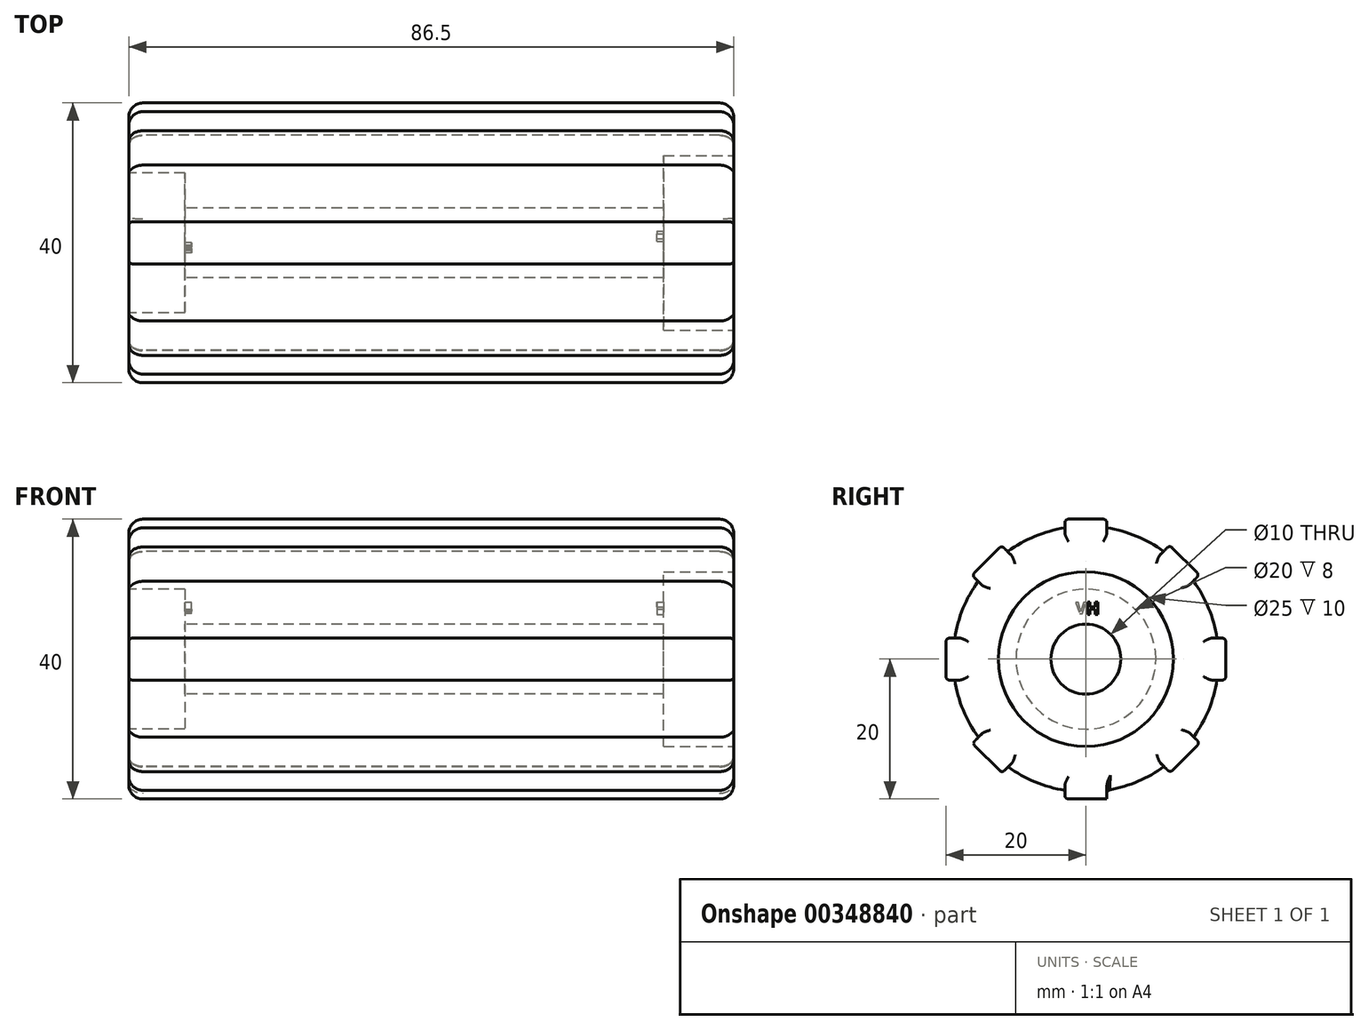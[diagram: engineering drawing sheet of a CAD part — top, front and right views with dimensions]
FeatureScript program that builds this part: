
annotation { "Feature Type Name" : "Feature", "Feature Type Description" : "" }
export const myFeature = defineFeature(function(context is Context, id is Id, definition is map)
    precondition{}
    {
        {
            var Q0;
            Q0=qCreatedBy(makeId("Right.planeOp"),FACE);
            var sketch = newSketch(context, id + "F0", { "sketchPlane" : qUnion([Q0])});
            skCircle(sketch, "E0", {"center": v(0, 0) * mm, "radius": 19 * mm});
            skCircle(sketch, "E1", {"center": v(0, 0) * mm, "radius": 5 * mm});
            skSolve(sketch);
        }
        {
            var Q0;
            Q0=makeQuery(id+"F0.imprint","IMPRINT",FACE,{"disambiguationData":[TD([[makeQuery(id+"F0.imprint","IMPRINT",EDGE,{"derivedFrom":sQuery(id+"F0.wireOp",EDGE,"E0")}),1.0]])]});
            extrude(context, id + "F1", {"entities" : qUnion([Q0]), "depth" : 86.5 * mm});
        }
        {
            var Q0;
            Q0=makeQuery(id+"F1.opExtrude","CAP_FACE",FACE,{"disambiguationData":[OSD([sQuery(id+"F0.wireOp",EDGE,"E0"),sQuery(id+"F0.wireOp",EDGE,"E1")])],"isStart":true});
            var sketch = newSketch(context, id + "F2", { "sketchPlane" : qUnion([Q0])});
            skCircle(sketch, "E2", {"center": v(0, 0) * mm, "radius": 10 * mm});
            skSolve(sketch);
        }
        {
            var Q0;
            Q0=makeQuery(id+"F2.imprint","IMPRINT",FACE,{"disambiguationData":[TD([[makeQuery(id+"F2.imprint","IMPRINT",EDGE,{"derivedFrom":sQuery(id+"F2.wireOp",EDGE,"E2")}),1.0]])]});
            extrude(context, id + "F3", {"entities" : qUnion([Q0]), "operationType" : NewBodyOperationType.REMOVE, "oppositeDirection" : true, "depth" : 8 * mm});
        }
        {
            var Q0;
            Q0=makeQuery(id+"F1.opExtrude","CAP_FACE",FACE,{"disambiguationData":[OSD([sQuery(id+"F0.wireOp",EDGE,"E0"),sQuery(id+"F0.wireOp",EDGE,"E1")])],"isStart":false});
            var sketch = newSketch(context, id + "F4", { "sketchPlane" : qUnion([Q0])});
            skCircle(sketch, "E3", {"center": v(0, 0) * mm, "radius": 10 * mm});
            skSolve(sketch);
        }
        {
            var Q0;
            Q0=makeQuery(id+"F4.imprint","IMPRINT",FACE,{"disambiguationData":[TD([[makeQuery(id+"F4.imprint","IMPRINT",EDGE,{"derivedFrom":sQuery(id+"F4.wireOp",EDGE,"E3")}),1.0]])]});
            extrude(context, id + "F5", {"entities" : qUnion([Q0]), "operationType" : NewBodyOperationType.REMOVE, "oppositeDirection" : true, "depth" : 10 * mm});
        }
        {
            var Q0;
            Q0=makeQuery(id+"F5.boolean.opBoolean","COPY",FACE,{"derivedFrom":makeQuery(id+"F5.opExtrude","CAP_FACE",FACE,{"disambiguationData":[OSD([sQuery(id+"F0.wireOp",EDGE,"E1"),sQuery(id+"F4.wireOp",EDGE,"E3")])],"isStart":false})});
            var sketch = newSketch(context, id + "F6", { "sketchPlane" : qUnion([Q0])});
            skText(sketch, "E4", { "text": "H", "fontName": "OpenSans-Bold.ttf"});
            const initialGuessF6  = {"E4": [0, 0.0064, 1, 0, 0.0018]};
            skSetInitialGuess(sketch, initialGuessF6);
            skSolve(sketch);
        }
        {
            var Q0;
            Q0=makeQuery(id+"F6.imprint","IMPRINT",FACE,{"disambiguationData":[TD([[makeQuery(id+"F6.imprint","IMPRINT",EDGE,{"derivedFrom":sQuery(id+"F6.wireOp",EDGE,"E4.sketch_text.stroke-0")}),-1.0]])]});
            extrude(context, id + "F7", {"entities" : qUnion([Q0]), "operationType" : NewBodyOperationType.REMOVE, "oppositeDirection" : true, "depth" : 1 * mm});
        }
        {
            var Q0;
            Q0=makeQuery(id+"F3.boolean.opBoolean","COPY",FACE,{"derivedFrom":makeQuery(id+"F3.opExtrude","CAP_FACE",FACE,{"disambiguationData":[OSD([sQuery(id+"F0.wireOp",EDGE,"E1"),sQuery(id+"F2.wireOp",EDGE,"E2")])],"isStart":false})});
            var sketch = newSketch(context, id + "F8", { "sketchPlane" : qUnion([Q0])});
            skText(sketch, "E5", { "text": "V", "fontName": "OpenSans-Bold.ttf"});
            const initialGuessF8  = {"E5": [0, 0.0065, 1, 0, 0.0016]};
            skSetInitialGuess(sketch, initialGuessF8);
            skSolve(sketch);
        }
        {
            var Q0;
            Q0 = qSketchRegion(id + "F8", true);
            extrude(context, id + "F9", {"entities" : qUnion([Q0]), "operationType" : NewBodyOperationType.REMOVE, "oppositeDirection" : true, "depth" : 1 * mm});
        }
        {
            var Q0;
            Q0=makeQuery(id+"F1.opExtrude","CAP_FACE",FACE,{"disambiguationData":[OSD([sQuery(id+"F0.wireOp",EDGE,"E0"),sQuery(id+"F0.wireOp",EDGE,"E1")])],"isStart":false});
            var sketch = newSketch(context, id + "F10", { "sketchPlane" : qUnion([Q0])});
            skCircle(sketch, "E6", {"center": v(0, 0) * mm, "radius": 12.5 * mm});
            skSolve(sketch);
        }
        {
            var Q0;
            Q0=makeQuery(id+"F10.imprint","IMPRINT",FACE,{"disambiguationData":[TD([[makeQuery(id+"F10.imprint","IMPRINT",EDGE,{"derivedFrom":sQuery(id+"F10.wireOp",EDGE,"E6")}),1.0]])]});
            extrude(context, id + "F11", {"entities" : qUnion([Q0]), "operationType" : NewBodyOperationType.REMOVE, "oppositeDirection" : true, "depth" : 10 * mm});
        }
        {
            var Q0;
            Q0=makeQuery(id+"F1.opExtrude","CAP_EDGE",EDGE,{"disambiguationData":[OSD([sQuery(id+"F0.wireOp",EDGE,"E0")])],"isStart":true});
            var Q1;
            Q1=makeQuery(id+"F1.opExtrude","CAP_EDGE",EDGE,{"disambiguationData":[OSD([sQuery(id+"F0.wireOp",EDGE,"E0")])],"isStart":false});
            fillet(context, id + "F12", {"entities" : qUnion([Q0, Q1]), "radius" : 2 * mm, "tangentPropagation" : true, "allowEdgeOverflow" : false});
        }
        {
            var Q0;
            Q0=makeQuery(id+"F1.opExtrude","CAP_FACE",FACE,{"disambiguationData":[OSD([sQuery(id+"F0.wireOp",EDGE,"E0"),sQuery(id+"F0.wireOp",EDGE,"E1")])],"isStart":false});
            var sketch = newSketch(context, id + "F13", { "sketchPlane" : qUnion([Q0])});
            skPoint(sketch, "E7.middle", {"position": v(0, 0) * mm});
            skLineSegment(sketch, "E8.top", {"start": v(-3, 14) * mm, "end": v(3, 14) * mm});
            skLineSegment(sketch, "E9.right", {"start": v(-14, 3) * mm, "end": v(-14, -3) * mm});
            skLineSegment(sketch, "E10.top", {"start": v(-3, -14) * mm, "end": v(3, -14) * mm});
            skPoint(sketch, "E11.endSnap0", {"position": v(-12, -12) * mm});
            skLineSegment(sketch, "E12", {"start": v(-7.8, 12) * mm, "end": v(-12.04, 7.75) * mm});
            skLineSegment(sketch, "E13", {"start": v(12, 7.8) * mm, "end": v(7.75, 12.04) * mm});
            skLineSegment(sketch, "E14", {"start": v(12.03, -7.76) * mm, "end": v(7.8, -12) * mm});
            skLineSegment(sketch, "E15", {"start": v(-7.76, -12.03) * mm, "end": v(-12, -7.8) * mm});
            skLineSegment(sketch, "E16", {"start": v(-20, 3) * mm, "end": v(-20, -3) * mm});
            skLineSegment(sketch, "E17", {"start": v(-20, 3) * mm, "end": v(-14, 3) * mm});
            skLineSegment(sketch, "E18", {"start": v(-20, -3) * mm, "end": v(-14, -3) * mm});
            skLineSegment(sketch, "E19", {"start": v(-12.04, 16.23) * mm, "end": v(-16.29, 12) * mm});
            skLineSegment(sketch, "E20", {"start": v(-12.04, 16.23) * mm, "end": v(-7.8, 12) * mm});
            skLineSegment(sketch, "E21", {"start": v(-16.29, 12) * mm, "end": v(-12.04, 7.75) * mm});
            skLineSegment(sketch, "E22.bottom", {"start": v(3, 20) * mm, "end": v(-3, 20) * mm});
            skLineSegment(sketch, "E22.top", {"start": v(3, 14) * mm, "end": v(-3, 14) * mm});
            skLineSegment(sketch, "E22.left", {"start": v(3, 20) * mm, "end": v(3, 14) * mm});
            skLineSegment(sketch, "E23", {"start": v(-3, 20) * mm, "end": v(-3, 14) * mm});
            skLineSegment(sketch, "E24", {"start": v(12, 16.29) * mm, "end": v(7.75, 12.04) * mm});
            skLineSegment(sketch, "E25", {"start": v(12, 16.29) * mm, "end": v(16.23, 12.04) * mm});
            skLineSegment(sketch, "E26", {"start": v(16.23, 12.04) * mm, "end": v(12, 7.8) * mm});
            skLineSegment(sketch, "E27", {"start": v(20, 3) * mm, "end": v(20, -3) * mm});
            skLineSegment(sketch, "E28.bottom", {"start": v(20, 3) * mm, "end": v(14, 3) * mm});
            skLineSegment(sketch, "E28.top", {"start": v(20, -3) * mm, "end": v(14, -3) * mm});
            skLineSegment(sketch, "E28.right", {"start": v(14, 3) * mm, "end": v(14, -3) * mm});
            skLineSegment(sketch, "E29", {"start": v(16.28, -12) * mm, "end": v(12.05, -16.24) * mm});
            skLineSegment(sketch, "E30", {"start": v(7.8, -12) * mm, "end": v(12.05, -16.24) * mm});
            skLineSegment(sketch, "E31", {"start": v(16.28, -12) * mm, "end": v(12.03, -7.76) * mm});
            skLineSegment(sketch, "E32", {"start": v(-16.24, -12.05) * mm, "end": v(-12, -16.28) * mm});
            skLineSegment(sketch, "E33", {"start": v(-12, -16.28) * mm, "end": v(-7.76, -12.03) * mm});
            skLineSegment(sketch, "E34", {"start": v(-12, -7.8) * mm, "end": v(-16.24, -12.05) * mm});
            skLineSegment(sketch, "E35", {"start": v(3, -20) * mm, "end": v(-3, -20) * mm});
            skLineSegment(sketch, "E36", {"start": v(-3, -20) * mm, "end": v(-3, -14) * mm});
            skLineSegment(sketch, "E37", {"start": v(3, -14) * mm, "end": v(3, -20) * mm});
            skSolve(sketch);
        }
        {
            var Q0;
            {var subQ0=sQuery(id+"F13.wireOp",EDGE,"E19");Q0=makeQuery(id+"F13.imprint","IMPRINT",FACE,{"disambiguationData":[TD([[makeQuery(id+"F13.imprint","IMPRINT",EDGE,{"derivedFrom":subQ0}),1.0]])]});}
            var Q1;
            {var subQ0=sQuery(id+"F13.wireOp",EDGE,"E22.bottom");Q1=makeQuery(id+"F13.imprint","IMPRINT",FACE,{"disambiguationData":[TD([[makeQuery(id+"F13.imprint","IMPRINT",EDGE,{"derivedFrom":subQ0}),1.0]])]});}
            var Q2;
            {var subQ0=sQuery(id+"F13.wireOp",EDGE,"E25");Q2=makeQuery(id+"F13.imprint","IMPRINT",FACE,{"disambiguationData":[TD([[makeQuery(id+"F13.imprint","IMPRINT",EDGE,{"derivedFrom":subQ0}),-1.0]])]});}
            var Q3;
            {var subQ0=sQuery(id+"F13.wireOp",EDGE,"E27");Q3=makeQuery(id+"F13.imprint","IMPRINT",FACE,{"disambiguationData":[TD([[makeQuery(id+"F13.imprint","IMPRINT",EDGE,{"derivedFrom":subQ0}),-1.0]])]});}
            var Q4;
            {var subQ0=sQuery(id+"F13.wireOp",EDGE,"E29");Q4=makeQuery(id+"F13.imprint","IMPRINT",FACE,{"disambiguationData":[TD([[makeQuery(id+"F13.imprint","IMPRINT",EDGE,{"derivedFrom":subQ0}),-1.0]])]});}
            var Q5;
            {var subQ0=sQuery(id+"F13.wireOp",EDGE,"E16");Q5=makeQuery(id+"F13.imprint","IMPRINT",FACE,{"disambiguationData":[TD([[makeQuery(id+"F13.imprint","IMPRINT",EDGE,{"derivedFrom":subQ0}),1.0]])]});}
            var Q6;
            {var subQ0=sQuery(id+"F13.wireOp",EDGE,"E35");Q6=makeQuery(id+"F13.imprint","IMPRINT",FACE,{"disambiguationData":[TD([[makeQuery(id+"F13.imprint","IMPRINT",EDGE,{"derivedFrom":subQ0}),-1.0]])]});}
            var Q7;
            {var subQ0=sQuery(id+"F13.wireOp",EDGE,"E32");Q7=makeQuery(id+"F13.imprint","IMPRINT",FACE,{"disambiguationData":[TD([[makeQuery(id+"F13.imprint","IMPRINT",EDGE,{"derivedFrom":subQ0}),1.0]])]});}
            extrude(context, id + "F14", {"entities" : qUnion([Q0, Q1, Q2, Q3, Q4, Q5, Q6, Q7]), "operationType" : NewBodyOperationType.ADD, "oppositeDirection" : true, "depth" : 86.5 * mm});
        }
        {
            var Q0;
            Q0=makeQuery(id+"F14.opExtrude","CAP_EDGE",EDGE,{"disambiguationData":[OSD([sQuery(id+"F13.wireOp",EDGE,"E19")])],"isStart":true});
            var Q1;
            Q1=makeQuery(id+"F14.opExtrude","CAP_EDGE",EDGE,{"disambiguationData":[OSD([sQuery(id+"F13.wireOp",EDGE,"E22.bottom")])],"isStart":true});
            var Q2;
            Q2=makeQuery(id+"F14.opExtrude","CAP_EDGE",EDGE,{"disambiguationData":[OSD([sQuery(id+"F13.wireOp",EDGE,"E25")])],"isStart":true});
            var Q3;
            Q3=makeQuery(id+"F14.opExtrude","CAP_EDGE",EDGE,{"disambiguationData":[OSD([sQuery(id+"F13.wireOp",EDGE,"E27")])],"isStart":true});
            var Q4;
            Q4=makeQuery(id+"F14.opExtrude","CAP_EDGE",EDGE,{"disambiguationData":[OSD([sQuery(id+"F13.wireOp",EDGE,"E29")])],"isStart":true});
            var Q5;
            Q5=makeQuery(id+"F14.opExtrude","CAP_EDGE",EDGE,{"disambiguationData":[OSD([sQuery(id+"F13.wireOp",EDGE,"E35")])],"isStart":true});
            var Q6;
            Q6=makeQuery(id+"F14.opExtrude","CAP_EDGE",EDGE,{"disambiguationData":[OSD([sQuery(id+"F13.wireOp",EDGE,"E32")])],"isStart":true});
            var Q7;
            Q7=makeQuery(id+"F14.opExtrude","CAP_EDGE",EDGE,{"disambiguationData":[OSD([sQuery(id+"F13.wireOp",EDGE,"E16")])],"isStart":true});
            var Q8;
            Q8=makeQuery(id+"F14.opExtrude","CAP_EDGE",EDGE,{"disambiguationData":[OSD([sQuery(id+"F13.wireOp",EDGE,"E25")])],"isStart":false});
            var Q9;
            Q9=makeQuery(id+"F14.opExtrude","CAP_EDGE",EDGE,{"disambiguationData":[OSD([sQuery(id+"F13.wireOp",EDGE,"E22.bottom")])],"isStart":false});
            var Q10;
            Q10=makeQuery(id+"F14.opExtrude","CAP_EDGE",EDGE,{"disambiguationData":[OSD([sQuery(id+"F13.wireOp",EDGE,"E19")])],"isStart":false});
            var Q11;
            Q11=makeQuery(id+"F14.opExtrude","CAP_EDGE",EDGE,{"disambiguationData":[OSD([sQuery(id+"F13.wireOp",EDGE,"E16")])],"isStart":false});
            var Q12;
            Q12=makeQuery(id+"F14.opExtrude","CAP_EDGE",EDGE,{"disambiguationData":[OSD([sQuery(id+"F13.wireOp",EDGE,"E32")])],"isStart":false});
            var Q13;
            Q13=makeQuery(id+"F14.opExtrude","CAP_EDGE",EDGE,{"disambiguationData":[OSD([sQuery(id+"F13.wireOp",EDGE,"E35")])],"isStart":false});
            var Q14;
            Q14=makeQuery(id+"F14.opExtrude","CAP_EDGE",EDGE,{"disambiguationData":[OSD([sQuery(id+"F13.wireOp",EDGE,"E29")])],"isStart":false});
            var Q15;
            Q15=makeQuery(id+"F14.opExtrude","CAP_EDGE",EDGE,{"disambiguationData":[OSD([sQuery(id+"F13.wireOp",EDGE,"E27")])],"isStart":false});
            fillet(context, id + "F15", {"entities" : qUnion([Q0, Q1, Q2, Q3, Q4, Q5, Q6, Q7, Q8, Q9, Q10, Q11, Q12, Q13, Q14, Q15]), "radius" : 2 * mm, "tangentPropagation" : true, "allowEdgeOverflow" : false});
        }
        {
            var Q0;
            Q0=makeQuery(id+"F14.opExtrude","SWEPT_EDGE",EDGE,{"disambiguationData":[OSD([sQuery(id+"F13.wireOp",EDGE,"E22.bottom"),sQuery(id+"F13.wireOp",EDGE,"E23")])]});
            var Q1;
            Q1=makeQuery(id+"F14.opExtrude","SWEPT_EDGE",EDGE,{"disambiguationData":[OSD([sQuery(id+"F13.wireOp",EDGE,"E19"),sQuery(id+"F13.wireOp",EDGE,"E21")])]});
            var Q2;
            Q2=makeQuery(id+"F14.opExtrude","SWEPT_EDGE",EDGE,{"disambiguationData":[OSD([sQuery(id+"F13.wireOp",EDGE,"E19"),sQuery(id+"F13.wireOp",EDGE,"E20")])]});
            var Q3;
            Q3=makeQuery(id+"F14.opExtrude","SWEPT_EDGE",EDGE,{"disambiguationData":[OSD([sQuery(id+"F13.wireOp",EDGE,"E16"),sQuery(id+"F13.wireOp",EDGE,"E17")])]});
            var Q4;
            Q4=makeQuery(id+"F14.opExtrude","SWEPT_EDGE",EDGE,{"disambiguationData":[OSD([sQuery(id+"F13.wireOp",EDGE,"E16"),sQuery(id+"F13.wireOp",EDGE,"E18")])]});
            var Q5;
            Q5=makeQuery(id+"F14.opExtrude","SWEPT_EDGE",EDGE,{"disambiguationData":[OSD([sQuery(id+"F13.wireOp",EDGE,"E22.bottom"),sQuery(id+"F13.wireOp",EDGE,"E22.left")])]});
            var Q6;
            Q6=makeQuery(id+"F14.opExtrude","SWEPT_EDGE",EDGE,{"disambiguationData":[OSD([sQuery(id+"F13.wireOp",EDGE,"E24"),sQuery(id+"F13.wireOp",EDGE,"E25")])]});
            var Q7;
            Q7=makeQuery(id+"F14.opExtrude","SWEPT_EDGE",EDGE,{"disambiguationData":[OSD([sQuery(id+"F13.wireOp",EDGE,"E25"),sQuery(id+"F13.wireOp",EDGE,"E26")])]});
            var Q8;
            Q8=makeQuery(id+"F14.opExtrude","SWEPT_EDGE",EDGE,{"disambiguationData":[OSD([sQuery(id+"F13.wireOp",EDGE,"E28.bottom"),sQuery(id+"F13.wireOp",EDGE,"E27")])]});
            var Q9;
            Q9=makeQuery(id+"F14.opExtrude","SWEPT_EDGE",EDGE,{"disambiguationData":[OSD([sQuery(id+"F13.wireOp",EDGE,"E28.top"),sQuery(id+"F13.wireOp",EDGE,"E27")])]});
            var Q10;
            Q10=makeQuery(id+"F14.opExtrude","SWEPT_EDGE",EDGE,{"disambiguationData":[OSD([sQuery(id+"F13.wireOp",EDGE,"E29"),sQuery(id+"F13.wireOp",EDGE,"E31")])]});
            var Q11;
            Q11=makeQuery(id+"F14.opExtrude","SWEPT_EDGE",EDGE,{"disambiguationData":[OSD([sQuery(id+"F13.wireOp",EDGE,"E29"),sQuery(id+"F13.wireOp",EDGE,"E30")])]});
            var Q12;
            Q12=makeQuery(id+"F14.boolean.opBoolean","INTERSECT",EDGE,{"derivedFrom":[makeQuery(id+"F1.opExtrude","SWEPT_FACE",FACE,{"disambiguationData":[OSD([sQuery(id+"F0.wireOp",EDGE,"E0")])]}),makeQuery(id+"F14.opExtrude","SWEPT_FACE",FACE,{"disambiguationData":[OSD([sQuery(id+"F13.wireOp",EDGE,"E37")])]})]});
            var Q13;
            Q13=makeQuery(id+"F14.opExtrude","SWEPT_EDGE",EDGE,{"disambiguationData":[OSD([sQuery(id+"F13.wireOp",EDGE,"E35"),sQuery(id+"F13.wireOp",EDGE,"E36")])]});
            var Q14;
            Q14=makeQuery(id+"F14.opExtrude","SWEPT_EDGE",EDGE,{"disambiguationData":[OSD([sQuery(id+"F13.wireOp",EDGE,"E32"),sQuery(id+"F13.wireOp",EDGE,"E33")])]});
            var Q15;
            Q15=makeQuery(id+"F14.opExtrude","SWEPT_EDGE",EDGE,{"disambiguationData":[OSD([sQuery(id+"F13.wireOp",EDGE,"E32"),sQuery(id+"F13.wireOp",EDGE,"E34")])]});
            fillet(context, id + "F16", {"entities" : qUnion([Q0, Q1, Q2, Q3, Q4, Q5, Q6, Q7, Q8, Q9, Q10, Q11, Q12, Q13, Q14, Q15]), "radius" : 0.5 * mm, "tangentPropagation" : true, "allowEdgeOverflow" : false});
        }
    });
